# Revit family: Windows_Blinds_Nimex_SC_100
name_source: partatom
category: Specialty Equipment
revit_build: Autodesk Revit 2018 (Build: 20190510_1515(x64)
units: mm (PartAtom-declared; Revit-internal decimal feet)

## family parameters
Cut with Voids When Loaded = No
Host = Face
OmniClass Number = 23.40.10.14
OmniClass Title = Exterior Specialties
Part Type = Normal
Room Calculation Point = No
Round Connector Dimension = Use Diameter
Shared = No

## types (1)
- SC 100
    AssetType = Fixed
    BIMObjectName = Windows_Blinds_Nimex_SC_100
    Brand = Elissi
    Category = Screens
    Color = Various
    Default Elevation = 0 mm  [stored 0 ft]
    DurationUnit = Years
    Features = Sun protection type Fiberglass-based screen weave.
    Finish = Profile color Lacquered aluminum profile. White, gray or black. Optional RAL color at extra cost. Material Plastic details in black or white.
    IfcExportAs = IfcShadingDeviceType
    IfcExportType = BLIND
    Manufacturer = Nimex
    ManufacturerName = Nimex
    ManufacturerURL = https://www.nimex.se
    Material = Aluminum & plastic
    Model = SC 100
    NBSDescription = Privacy screen system
    NBSReference = 25-05-60/165
    Name = Nimex_SC_100
    NominalDepth = 100 mm  [stored 0.328084 ft]
    Shape = Sculptured
    Size = 2700x100x2700 mm
    URL = https://elissi.se
    Uniclass2 = Ss_25_12_60_65
    Uniclass2015Description = Privacy screen systems
    Uniclass2015Reference = Ss_25_12_60_65
    Version = 1
    VersionDate = 15/04/2021
    WarrantyDurationUnit = Years

note: [stored X ft] marks values corroborated as IEEE doubles in the binary element streams (Revit-internal decimal feet)

## geometry (parser evidence)
native form markers: Sweep x12
no freeform markers — native parametric forms only
